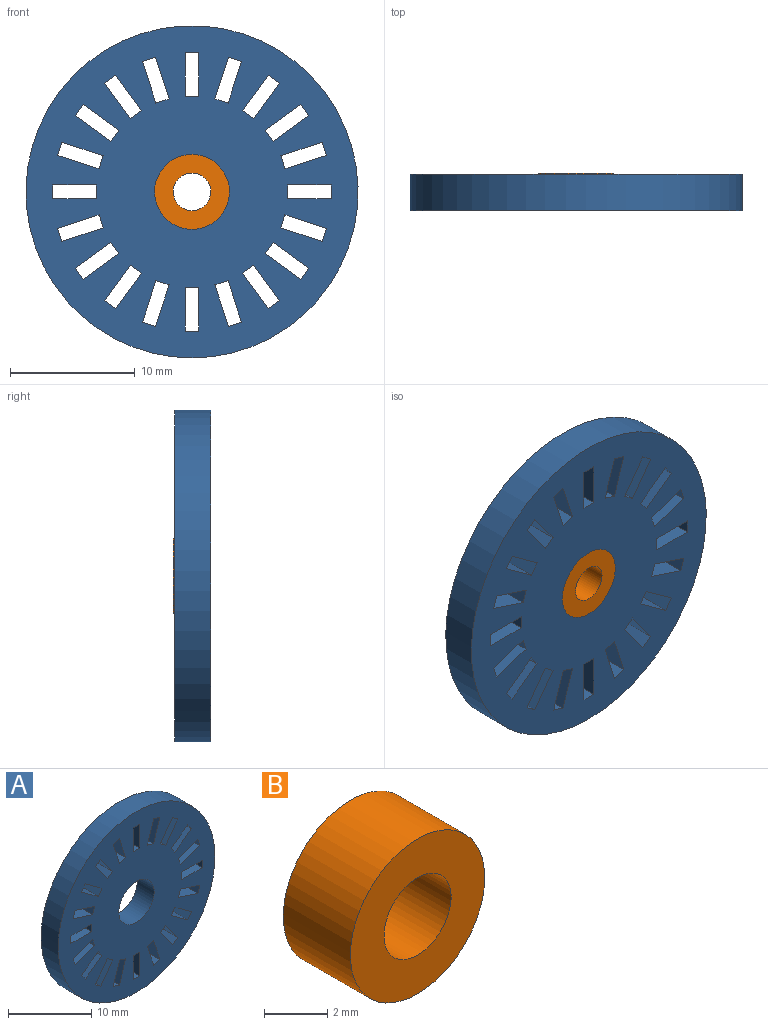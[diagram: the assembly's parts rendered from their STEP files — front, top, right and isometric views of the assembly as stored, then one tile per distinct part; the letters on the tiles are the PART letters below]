
ASSEMBLY  parts=2 mates=1
PART A: 84 faces, bbox 26.6x2.9x26.6 mm
  f0: cylinder r=3mm len=6mm, axis (0,1,0), area 54.7mm2, adj f2,f3
  f1: cylinder r=13.3mm len=26.6mm, axis (0,1,0), area 242.3mm2, adj f2,f3
  f2: plane 26.6x26.6mm, normal (0,-1,0), area 450.4mm2, adj f0,f1,f4,f5,f6,f7,f8,f9
  f3: plane 26.6x26.6mm, normal (0,1,0), area 450.4mm2, adj f0,f1,f4,f5,f6,f7,f8,f9
  f4: plane 2.9x1.1mm, normal (-1,0,0), area 3.2mm2, adj f2,f3,f5,f7
  f5: plane 3.5x2.9mm, normal (0,0,-1), area 10.1mm2, adj f2,f3,f4,f6
  f6: plane 2.9x1.1mm, normal (1,0,0), area 3.2mm2, adj f2,f3,f5,f7
  f7: plane 3.5x2.9mm, normal (0,0,1), area 10.1mm2, adj f2,f3,f4,f6
  f8: plane 2.9x1.05mm, normal (-0.95,0,-0.31), area 3.2mm2, adj f2,f3,f9,f11
  f9: plane 3.33x2.9mm, normal (0.31,0,-0.95), area 10.2mm2, adj f2,f3,f8,f10
  f10: plane 2.9x1.05mm, normal (0.95,0,0.31), area 3.2mm2, adj f2,f3,f9,f11
  f11: plane 3.33x2.9mm, normal (-0.31,0,0.95), area 10.2mm2, adj f2,f3,f8,f10
  f12: plane 2.9x0.89mm, normal (-0.81,0,-0.59), area 3.2mm2, adj f2,f3,f13,f15
  f13: plane 2.9x2.83mm, normal (0.59,0,-0.81), area 10.2mm2, adj f2,f3,f12,f14
  f14: plane 2.9x0.89mm, normal (0.81,0,0.59), area 3.2mm2, adj f2,f3,f13,f15
  f15: plane 2.9x2.83mm, normal (-0.59,0,0.81), area 10.1mm2, adj f2,f3,f12,f14
  f16: plane 2.9x0.89mm, normal (-0.59,0,-0.81), area 3.2mm2, adj f2,f3,f17,f19
  f17: plane 2.9x2.83mm, normal (0.81,0,-0.59), area 10.1mm2, adj f2,f3,f16,f18
  f18: plane 2.9x0.89mm, normal (0.59,0,0.81), area 3.2mm2, adj f2,f3,f17,f19
  f19: plane 2.9x2.83mm, normal (-0.81,0,0.59), area 10.2mm2, adj f2,f3,f16,f18
  f20: plane 2.9x1.05mm, normal (-0.31,0,-0.95), area 3.2mm2, adj f2,f3,f21,f23
  f21: plane 3.33x2.9mm, normal (0.95,0,-0.31), area 10.2mm2, adj f2,f3,f20,f22
  f22: plane 2.9x1.05mm, normal (0.31,0,0.95), area 3.2mm2, adj f2,f3,f21,f23
  f23: plane 3.33x2.9mm, normal (-0.95,0,0.31), area 10.2mm2, adj f2,f3,f20,f22
  f24: plane 2.9x1.1mm, normal (0,0,-1), area 3.2mm2, adj f2,f3,f25,f27
  f25: plane 3.5x2.9mm, normal (1,0,0), area 10.1mm2, adj f2,f3,f24,f26
  f26: plane 2.9x1.1mm, normal (0,0,1), area 3.2mm2, adj f2,f3,f25,f27
  f27: plane 3.5x2.9mm, normal (-1,0,0), area 10.1mm2, adj f2,f3,f24,f26
  f28: plane 2.9x1.05mm, normal (0.31,0,-0.95), area 3.2mm2, adj f2,f3,f29,f31
  f29: plane 3.33x2.9mm, normal (0.95,0,0.31), area 10.2mm2, adj f2,f3,f28,f30
  f30: plane 2.9x1.05mm, normal (-0.31,0,0.95), area 3.2mm2, adj f2,f3,f29,f31
  f31: plane 3.33x2.9mm, normal (-0.95,0,-0.31), area 10.2mm2, adj f2,f3,f28,f30
  f32: plane 2.9x0.89mm, normal (0.59,0,-0.81), area 3.2mm2, adj f2,f3,f33,f35
  f33: plane 2.9x2.83mm, normal (0.81,0,0.59), area 10.2mm2, adj f2,f3,f32,f34
  f34: plane 2.9x0.89mm, normal (-0.59,0,0.81), area 3.2mm2, adj f2,f3,f33,f35
  f35: plane 2.9x2.83mm, normal (-0.81,0,-0.59), area 10.1mm2, adj f2,f3,f32,f34
  f36: plane 2.9x0.89mm, normal (0.81,0,-0.59), area 3.2mm2, adj f2,f3,f37,f39
  f37: plane 2.9x2.83mm, normal (0.59,0,0.81), area 10.1mm2, adj f2,f3,f36,f38
  f38: plane 2.9x0.89mm, normal (-0.81,0,0.59), area 3.2mm2, adj f2,f3,f37,f39
  f39: plane 2.9x2.83mm, normal (-0.59,0,-0.81), area 10.2mm2, adj f2,f3,f36,f38
  f40: plane 2.9x1.05mm, normal (0.95,0,-0.31), area 3.2mm2, adj f2,f3,f41,f43
  f41: plane 3.33x2.9mm, normal (0.31,0,0.95), area 10.2mm2, adj f2,f3,f40,f42
  f42: plane 2.9x1.05mm, normal (-0.95,0,0.31), area 3.2mm2, adj f2,f3,f41,f43
  f43: plane 3.33x2.9mm, normal (-0.31,0,-0.95), area 10.2mm2, adj f2,f3,f40,f42
  f44: plane 2.9x1.1mm, normal (1,0,0), area 3.2mm2, adj f2,f3,f45,f47
  f45: plane 3.5x2.9mm, normal (0,0,1), area 10.1mm2, adj f2,f3,f44,f46
  f46: plane 2.9x1.1mm, normal (-1,0,0), area 3.2mm2, adj f2,f3,f45,f47
  f47: plane 3.5x2.9mm, normal (0,0,-1), area 10.1mm2, adj f2,f3,f44,f46
  f48: plane 2.9x1.05mm, normal (0.95,0,0.31), area 3.2mm2, adj f2,f3,f49,f51
  f49: plane 3.33x2.9mm, normal (-0.31,0,0.95), area 10.2mm2, adj f2,f3,f48,f50
  f50: plane 2.9x1.05mm, normal (-0.95,0,-0.31), area 3.2mm2, adj f2,f3,f49,f51
  f51: plane 3.33x2.9mm, normal (0.31,0,-0.95), area 10.2mm2, adj f2,f3,f48,f50
  f52: plane 2.9x0.89mm, normal (0.81,0,0.59), area 3.2mm2, adj f2,f3,f53,f55
  f53: plane 2.9x2.83mm, normal (-0.59,0,0.81), area 10.2mm2, adj f2,f3,f52,f54
  f54: plane 2.9x0.89mm, normal (-0.81,0,-0.59), area 3.2mm2, adj f2,f3,f53,f55
  f55: plane 2.9x2.83mm, normal (0.59,0,-0.81), area 10.1mm2, adj f2,f3,f52,f54
  f56: plane 2.9x0.89mm, normal (0.59,0,0.81), area 3.2mm2, adj f2,f3,f57,f59
  f57: plane 2.9x2.83mm, normal (-0.81,0,0.59), area 10.1mm2, adj f2,f3,f56,f58
  f58: plane 2.9x0.89mm, normal (-0.59,0,-0.81), area 3.2mm2, adj f2,f3,f57,f59
  f59: plane 2.9x2.83mm, normal (0.81,0,-0.59), area 10.2mm2, adj f2,f3,f56,f58
  f60: plane 2.9x1.05mm, normal (0.31,0,0.95), area 3.2mm2, adj f2,f3,f61,f63
  f61: plane 3.33x2.9mm, normal (-0.95,0,0.31), area 10.2mm2, adj f2,f3,f60,f62
  f62: plane 2.9x1.05mm, normal (-0.31,0,-0.95), area 3.2mm2, adj f2,f3,f61,f63
  f63: plane 3.33x2.9mm, normal (0.95,0,-0.31), area 10.2mm2, adj f2,f3,f60,f62
  f64: plane 2.9x1.1mm, normal (0,0,1), area 3.2mm2, adj f2,f3,f65,f67
  f65: plane 3.5x2.9mm, normal (-1,0,0), area 10.1mm2, adj f2,f3,f64,f66
  f66: plane 2.9x1.1mm, normal (0,0,-1), area 3.2mm2, adj f2,f3,f65,f67
  f67: plane 3.5x2.9mm, normal (1,0,0), area 10.1mm2, adj f2,f3,f64,f66
  f68: plane 2.9x1.05mm, normal (-0.31,0,0.95), area 3.2mm2, adj f2,f3,f69,f71
  f69: plane 3.33x2.9mm, normal (-0.95,0,-0.31), area 10.2mm2, adj f2,f3,f68,f70
  f70: plane 2.9x1.05mm, normal (0.31,0,-0.95), area 3.2mm2, adj f2,f3,f69,f71
  f71: plane 3.33x2.9mm, normal (0.95,0,0.31), area 10.2mm2, adj f2,f3,f68,f70
  f72: plane 2.9x0.89mm, normal (-0.59,0,0.81), area 3.2mm2, adj f2,f3,f73,f75
  f73: plane 2.9x2.83mm, normal (-0.81,0,-0.59), area 10.2mm2, adj f2,f3,f72,f74
  f74: plane 2.9x0.89mm, normal (0.59,0,-0.81), area 3.2mm2, adj f2,f3,f73,f75
  f75: plane 2.9x2.83mm, normal (0.81,0,0.59), area 10.1mm2, adj f2,f3,f72,f74
  f76: plane 2.9x0.89mm, normal (-0.81,0,0.59), area 3.2mm2, adj f2,f3,f77,f79
  f77: plane 2.9x2.83mm, normal (-0.59,0,-0.81), area 10.1mm2, adj f2,f3,f76,f78
  f78: plane 2.9x0.89mm, normal (0.81,0,-0.59), area 3.2mm2, adj f2,f3,f77,f79
  f79: plane 2.9x2.83mm, normal (0.59,0,0.81), area 10.2mm2, adj f2,f3,f76,f78
  f80: plane 2.9x1.05mm, normal (-0.95,0,0.31), area 3.2mm2, adj f2,f3,f81,f83
  f81: plane 3.33x2.9mm, normal (-0.31,0,-0.95), area 10.2mm2, adj f2,f3,f80,f82
  f82: plane 2.9x1.05mm, normal (0.95,0,-0.31), area 3.2mm2, adj f2,f3,f81,f83
  f83: plane 3.33x2.9mm, normal (0.31,0,0.95), area 10.2mm2, adj f2,f3,f80,f82
PART B: 4 faces, bbox 6x3x6 mm
  f0: cylinder r=1.5mm len=3mm, axis (0,1,0), area 28.3mm2, adj f2,f3
  f1: cylinder r=3mm len=6mm, axis (0,1,0), area 56.5mm2, adj f2,f3
  f2: plane 6x6mm, normal (0,-1,0), area 21.2mm2, adj f0,f1
  f3: plane 6x6mm, normal (0,1,0), area 21.2mm2, adj f0,f1
PLACE A t=(-1.46,0.67,0.09)mm
PLACE B t=(-1.46,0.77,0.09)mm
MATE fastened B.f1 <-> A.f1  axis (0,-1,0) through (-1.46,-2.23,0.09)mm
